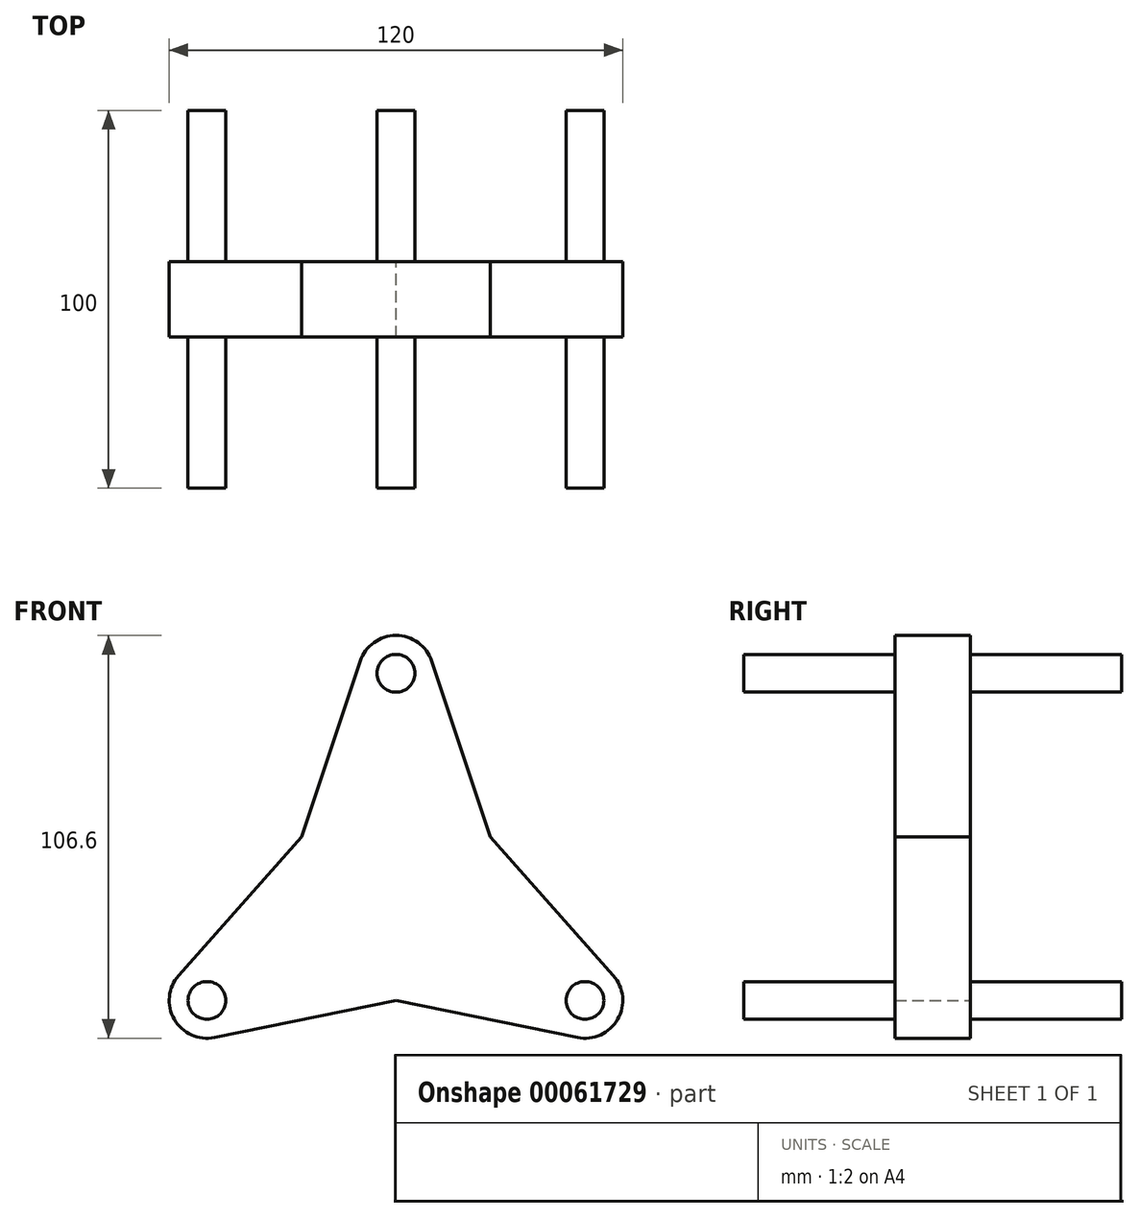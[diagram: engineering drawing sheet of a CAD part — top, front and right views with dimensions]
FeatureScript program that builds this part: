
annotation { "Feature Type Name" : "Feature", "Feature Type Description" : "" }
export const myFeature = defineFeature(function(context is Context, id is Id, definition is map)
    precondition{}
    {
        {
            var Q0;
            Q0=qCreatedBy(makeId("Front.planeOp"),FACE);
            var sketch = newSketch(context, id + "F0", { "sketchPlane" : qUnion([Q0])});
            skLineSegment(sketch, "E0", {"start": v(0, 0) * mm, "end": v(-50, -86.6) * mm});
            skLineSegment(sketch, "E1", {"start": v(-50, -86.6) * mm, "end": v(50, -86.6) * mm});
            skLineSegment(sketch, "E2", {"start": v(50, -86.6) * mm, "end": v(0, 0) * mm});
            skCircle(sketch, "E3", {"center": v(0, 0) * mm, "radius": 10 * mm});
            skCircle(sketch, "E4", {"center": v(0, 0) * mm, "radius": 5 * mm});
            skCircle(sketch, "E5", {"center": v(-50, -86.6) * mm, "radius": 5 * mm});
            skCircle(sketch, "E6", {"center": v(-50, -86.6) * mm, "radius": 10 * mm});
            skCircle(sketch, "E7", {"center": v(50, -86.6) * mm, "radius": 5 * mm});
            skCircle(sketch, "E8", {"center": v(50, -86.6) * mm, "radius": 10 * mm});
            skLineSegment(sketch, "E9", {"start": v(-25, -43.3) * mm, "end": v(-9.49, 3.17) * mm});
            skLineSegment(sketch, "E10", {"start": v(-57.49, -79.97) * mm, "end": v(-25, -43.3) * mm});
            skLineSegment(sketch, "E11", {"start": v(25, -43.3) * mm, "end": v(9.49, 3.17) * mm});
            skLineSegment(sketch, "E12", {"start": v(25, -43.3) * mm, "end": v(57.49, -79.97) * mm});
            skLineSegment(sketch, "E13", {"start": v(0, -86.6) * mm, "end": v(48, -96.4) * mm});
            skLineSegment(sketch, "E14", {"start": v(0, -86.6) * mm, "end": v(-48, -96.4) * mm});
            skSolve(sketch);
        }
        {
            var Q0;
            Q0 = qSketchRegion(id + "F0", true);
            var Q1;
            {var subQ0=sQuery(id+"F0.wireOp",EDGE,"E4");var subQ1=sQuery(id+"F0.wireOp",EDGE,"E0");var subQ2=makeQuery(id+"F0.imprint","INTERSECT",VERTEX,{"derivedFrom":[subQ1,subQ0]});Q1=makeQuery(id+"F0.imprint","IMPRINT",FACE,{"disambiguationData":[TD([[makeQuery(id+"F0.imprint","IMPRINT",EDGE,{"disambiguationData":[TD([[subQ2,-1.0]])],"derivedFrom":subQ1}),1.0]])]});}
            var Q2;
            {var subQ0=sQuery(id+"F0.wireOp",EDGE,"E6");var subQ1=sQuery(id+"F0.wireOp",EDGE,"E0");var subQ2=makeQuery(id+"F0.imprint","INTERSECT",VERTEX,{"derivedFrom":[subQ1,subQ0]});Q2=makeQuery(id+"F0.imprint","IMPRINT",FACE,{"disambiguationData":[TD([[makeQuery(id+"F0.imprint","IMPRINT",EDGE,{"disambiguationData":[TD([[subQ2,-1.0]])],"derivedFrom":subQ1}),1.0]])]});}
            var Q3;
            {var subQ0=sQuery(id+"F0.wireOp",EDGE,"E8");var subQ1=sQuery(id+"F0.wireOp",EDGE,"E1");var subQ2=makeQuery(id+"F0.imprint","INTERSECT",VERTEX,{"derivedFrom":[subQ1,subQ0]});Q3=makeQuery(id+"F0.imprint","IMPRINT",FACE,{"disambiguationData":[TD([[makeQuery(id+"F0.imprint","IMPRINT",EDGE,{"disambiguationData":[TD([[subQ2,-1.0]])],"derivedFrom":subQ1}),1.0]])]});}
            extrude(context, id + "F1", {"entities" : qUnion([Q0, Q1, Q2, Q3]), "endBound" : BoundingType.SYMMETRIC, "depth" : 20 * mm});
        }
        {
            var Q0;
            {var subQ0=sQuery(id+"F0.wireOp",EDGE,"E2");var subQ1=sQuery(id+"F0.wireOp",EDGE,"E0");var subQ2=makeQuery(id+"F0.imprint","INTERSECT",VERTEX,{"derivedFrom":[subQ1,subQ0]});Q0=makeQuery(id+"F0.imprint","IMPRINT",FACE,{"disambiguationData":[TD([[makeQuery(id+"F0.imprint","IMPRINT",EDGE,{"disambiguationData":[TD([[subQ2,-1.0]])],"derivedFrom":subQ1}),-1.0]])]});}
            var Q1;
            {var subQ0=sQuery(id+"F0.wireOp",EDGE,"E2");var subQ1=sQuery(id+"F0.wireOp",EDGE,"E0");var subQ2=makeQuery(id+"F0.imprint","INTERSECT",VERTEX,{"derivedFrom":[subQ1,subQ0]});Q1=makeQuery(id+"F0.imprint","IMPRINT",FACE,{"disambiguationData":[TD([[makeQuery(id+"F0.imprint","IMPRINT",EDGE,{"disambiguationData":[TD([[subQ2,-1.0]])],"derivedFrom":subQ1}),1.0]])]});}
            var Q2;
            {var subQ0=sQuery(id+"F0.wireOp",EDGE,"E1");var subQ1=sQuery(id+"F0.wireOp",EDGE,"E0");var subQ2=makeQuery(id+"F0.imprint","INTERSECT",VERTEX,{"derivedFrom":[subQ1,subQ0]});Q2=makeQuery(id+"F0.imprint","IMPRINT",FACE,{"disambiguationData":[TD([[makeQuery(id+"F0.imprint","IMPRINT",EDGE,{"disambiguationData":[TD([[subQ2,1.0]])],"derivedFrom":subQ1}),-1.0]])]});}
            var Q3;
            {var subQ0=sQuery(id+"F0.wireOp",EDGE,"E1");var subQ1=sQuery(id+"F0.wireOp",EDGE,"E0");var subQ2=makeQuery(id+"F0.imprint","INTERSECT",VERTEX,{"derivedFrom":[subQ1,subQ0]});Q3=makeQuery(id+"F0.imprint","IMPRINT",FACE,{"disambiguationData":[TD([[makeQuery(id+"F0.imprint","IMPRINT",EDGE,{"disambiguationData":[TD([[subQ2,1.0]])],"derivedFrom":subQ1}),1.0]])]});}
            var Q4;
            {var subQ0=sQuery(id+"F0.wireOp",EDGE,"E2");var subQ1=sQuery(id+"F0.wireOp",EDGE,"E1");var subQ2=makeQuery(id+"F0.imprint","INTERSECT",VERTEX,{"derivedFrom":[subQ1,subQ0]});Q4=makeQuery(id+"F0.imprint","IMPRINT",FACE,{"disambiguationData":[TD([[makeQuery(id+"F0.imprint","IMPRINT",EDGE,{"disambiguationData":[TD([[subQ2,1.0]])],"derivedFrom":subQ1}),1.0]])]});}
            var Q5;
            {var subQ0=sQuery(id+"F0.wireOp",EDGE,"E2");var subQ1=sQuery(id+"F0.wireOp",EDGE,"E1");var subQ2=makeQuery(id+"F0.imprint","INTERSECT",VERTEX,{"derivedFrom":[subQ1,subQ0]});Q5=makeQuery(id+"F0.imprint","IMPRINT",FACE,{"disambiguationData":[TD([[makeQuery(id+"F0.imprint","IMPRINT",EDGE,{"disambiguationData":[TD([[subQ2,1.0]])],"derivedFrom":subQ1}),-1.0]])]});}
            var Q6;
            Q6=sQuery(id+"F0.wireOp",EDGE,"E4");
            extrude(context, id + "F2", {"entities" : qUnion([Q0, Q1, Q2, Q3, Q4, Q5]), "operationType" : NewBodyOperationType.ADD, "surfaceEntities" : qUnion([Q6]), "endBound" : BoundingType.SYMMETRIC, "depth" : 100 * mm});
        }
    });
